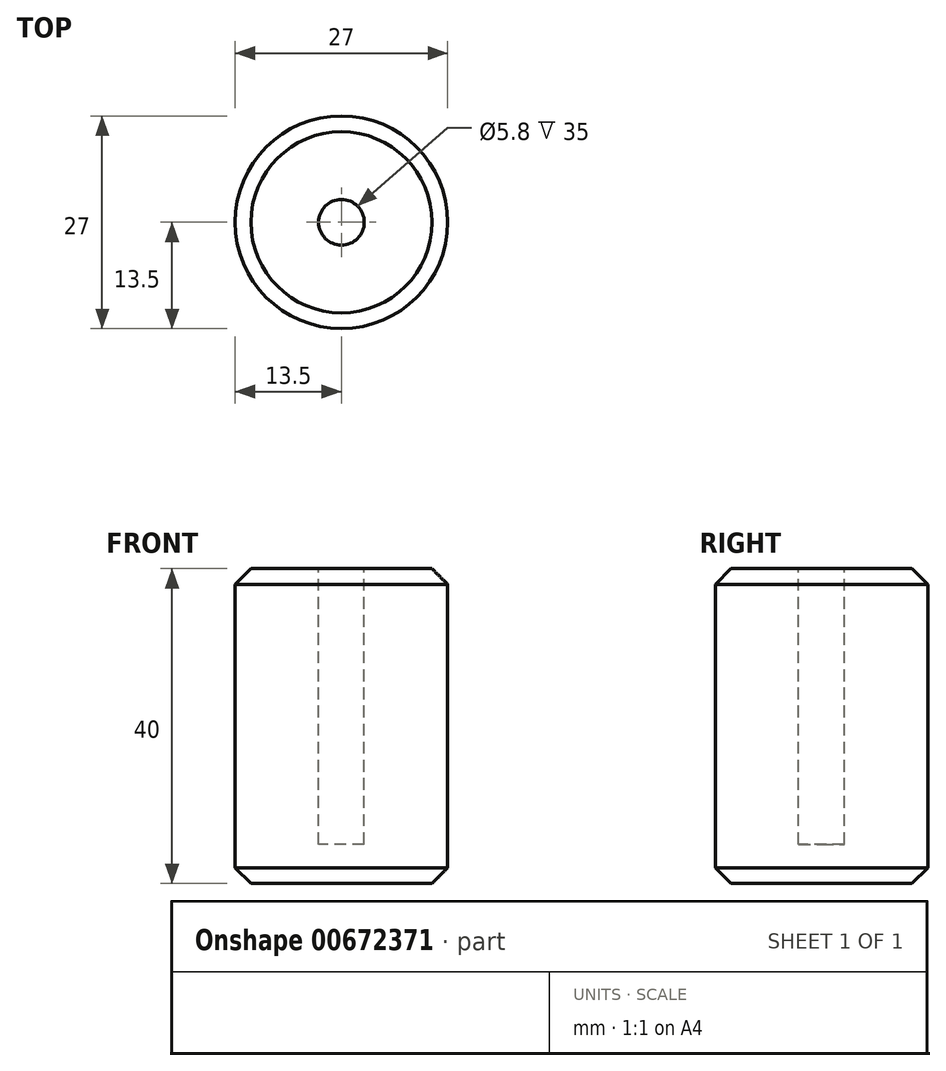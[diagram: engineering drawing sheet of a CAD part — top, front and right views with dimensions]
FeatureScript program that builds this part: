
annotation { "Feature Type Name" : "Feature", "Feature Type Description" : "" }
export const myFeature = defineFeature(function(context is Context, id is Id, definition is map)
    precondition{}
    {
        {
            var Q0;
            Q0=qCreatedBy(makeId("Top.planeOp"),FACE);
            var sketch = newSketch(context, id + "F0", { "sketchPlane" : qUnion([Q0])});
            skCircle(sketch, "E0", {"center": v(0, 0) * mm, "radius": 13.5 * mm});
            skSolve(sketch);
        }
        {
            var Q0;
            Q0 = qSketchRegion(id + "F0", true);
            extrude(context, id + "F1", {"entities" : qUnion([Q0]), "depth" : 40 * mm, "offsetDistance" : 25 * mm});
        }
        {
            var Q0;
            Q0=makeQuery(id+"F1.opExtrude","CAP_FACE",FACE,{"disambiguationData":[OSD([sQuery(id+"F0.wireOp",EDGE,"E0")])],"isStart":false});
            var sketch = newSketch(context, id + "F2", { "sketchPlane" : qUnion([Q0])});
            skCircle(sketch, "E1", {"center": v(0, 0) * mm, "radius": 2.9 * mm});
            skSolve(sketch);
        }
        {
            var Q0;
            Q0 = qSketchRegion(id + "F2", true);
            extrude(context, id + "F3", {"entities" : qUnion([Q0]), "operationType" : NewBodyOperationType.REMOVE, "oppositeDirection" : true, "depth" : 35 * mm, "offsetDistance" : 25 * mm});
        }
        {
            var Q0;
            Q0=makeQuery(id+"F1.opExtrude","CAP_EDGE",EDGE,{"disambiguationData":[OSD([sQuery(id+"F0.wireOp",EDGE,"E0")])],"isStart":true});
            var Q1;
            Q1=makeQuery(id+"F1.opExtrude","CAP_EDGE",EDGE,{"disambiguationData":[OSD([sQuery(id+"F0.wireOp",EDGE,"E0")])],"isStart":false});
            chamfer(context, id + "F4", {"entities" : qUnion([Q0, Q1]), "width" : 2 * mm, "tangentPropagation" : true});
        }
    });
